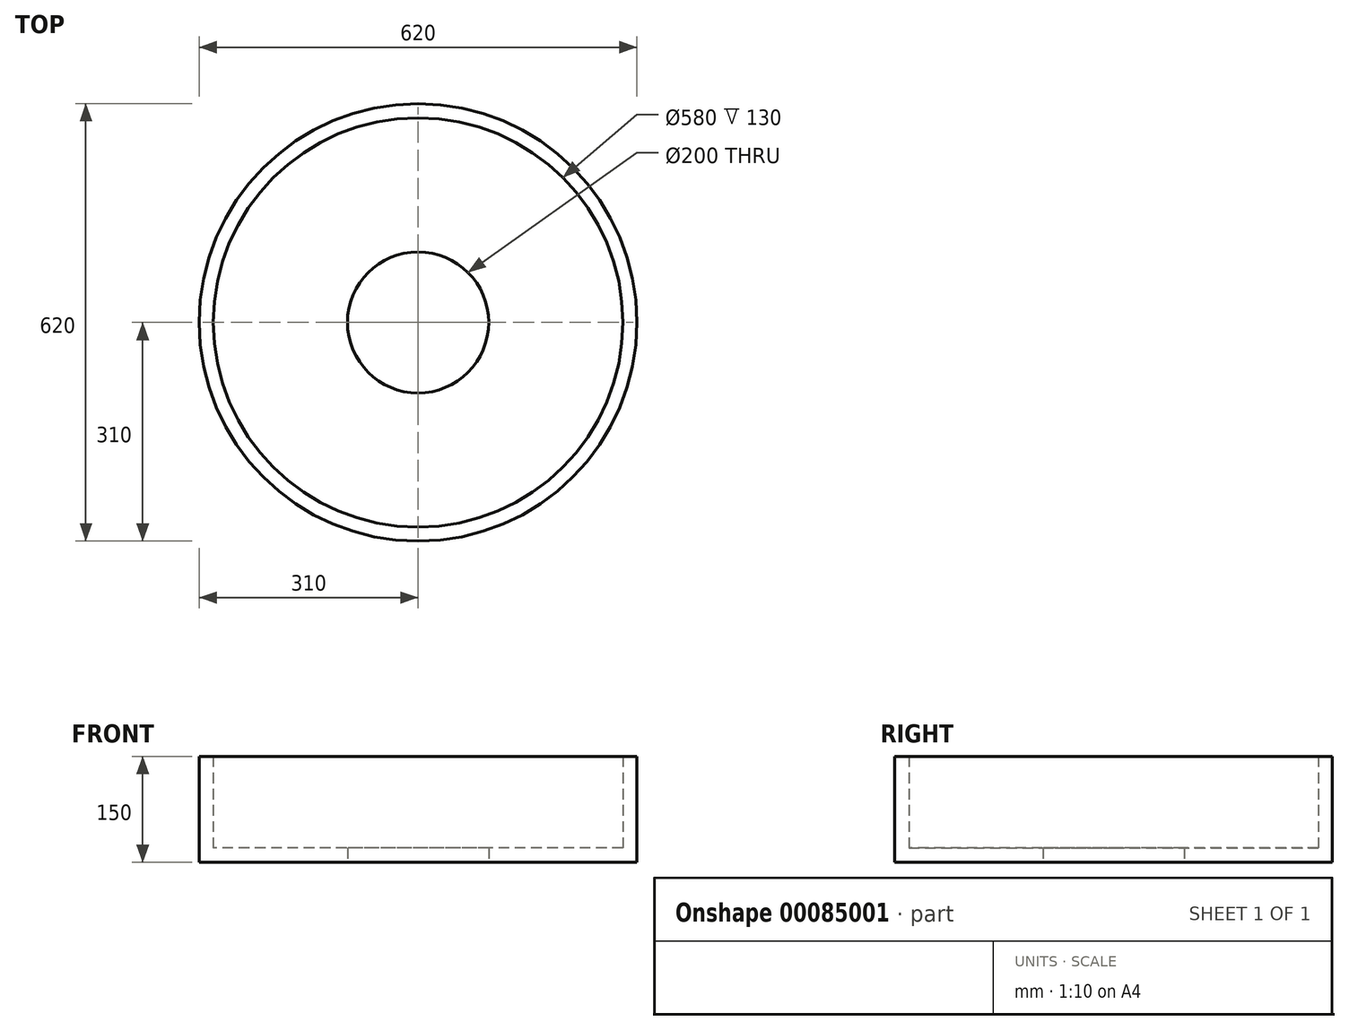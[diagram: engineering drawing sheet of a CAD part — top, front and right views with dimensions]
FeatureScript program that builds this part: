
annotation { "Feature Type Name" : "Feature", "Feature Type Description" : "" }
export const myFeature = defineFeature(function(context is Context, id is Id, definition is map)
    precondition{}
    {
        {
            var Q0;
            Q0=qCreatedBy(makeId("Top.planeOp"),FACE);
            var sketch = newSketch(context, id + "F0", { "sketchPlane" : qUnion([Q0])});
            skCircle(sketch, "E0", {"center": v(0, 0) * mm, "radius": 290 * mm});
            skLineSegment(sketch, "E1", {"start": v(0, 0) * mm, "end": v(126.13, 261.13) * mm});
            skCircle(sketch, "E2", {"center": v(0, 0) * mm, "radius": 310 * mm});
            skLineSegment(sketch, "E3", {"start": v(0, 0) * mm, "end": v(257.58, 172.48) * mm});
            skCircle(sketch, "E4", {"center": v(0, 0) * mm, "radius": 100 * mm});
            skLineSegment(sketch, "E5", {"start": v(0, 0) * mm, "end": v(98.42, 17.7) * mm});
            skSolve(sketch);
        }
        {
            var Q0;
            Q0 = qSketchRegion(id + "F0", true);
            extrude(context, id + "F1", {"entities" : qUnion([Q0]), "depth" : 150 * mm});
        }
        {
            var Q0;
            Q0 = qSketchRegion(id + "F0", true);
            var Q1;
            {var subQ4=sQuery(id+"F0.wireOp",EDGE,"E0");var subQ6=sQuery(id+"F0.wireOp",EDGE,"E1");var subQ7=makeQuery(id+"F0.imprint","INTERSECT",VERTEX,{"derivedFrom":[subQ4,subQ6]});Q1=makeQuery(id+"F0.imprint","IMPRINT",FACE,{"disambiguationData":[TD([[makeQuery(id+"F0.imprint","IMPRINT",EDGE,{"disambiguationData":[TD([[subQ7,-1.0]])],"derivedFrom":subQ4}),1.0]])]});}
            var Q2;
            {var subQ0=sQuery(id+"F0.wireOp",EDGE,"E1");var subQ1=sQuery(id+"F0.wireOp",EDGE,"E0");var subQ2=makeQuery(id+"F0.imprint","INTERSECT",VERTEX,{"derivedFrom":[subQ1,subQ0]});Q2=makeQuery(id+"F0.imprint","IMPRINT",FACE,{"disambiguationData":[TD([[makeQuery(id+"F0.imprint","IMPRINT",EDGE,{"disambiguationData":[TD([[subQ2,1.0]])],"derivedFrom":subQ1}),1.0]])]});}
            extrude(context, id + "F2", {"entities" : qUnion([Q0, Q1, Q2]), "operationType" : NewBodyOperationType.ADD, "depth" : 20 * mm});
        }
    });
